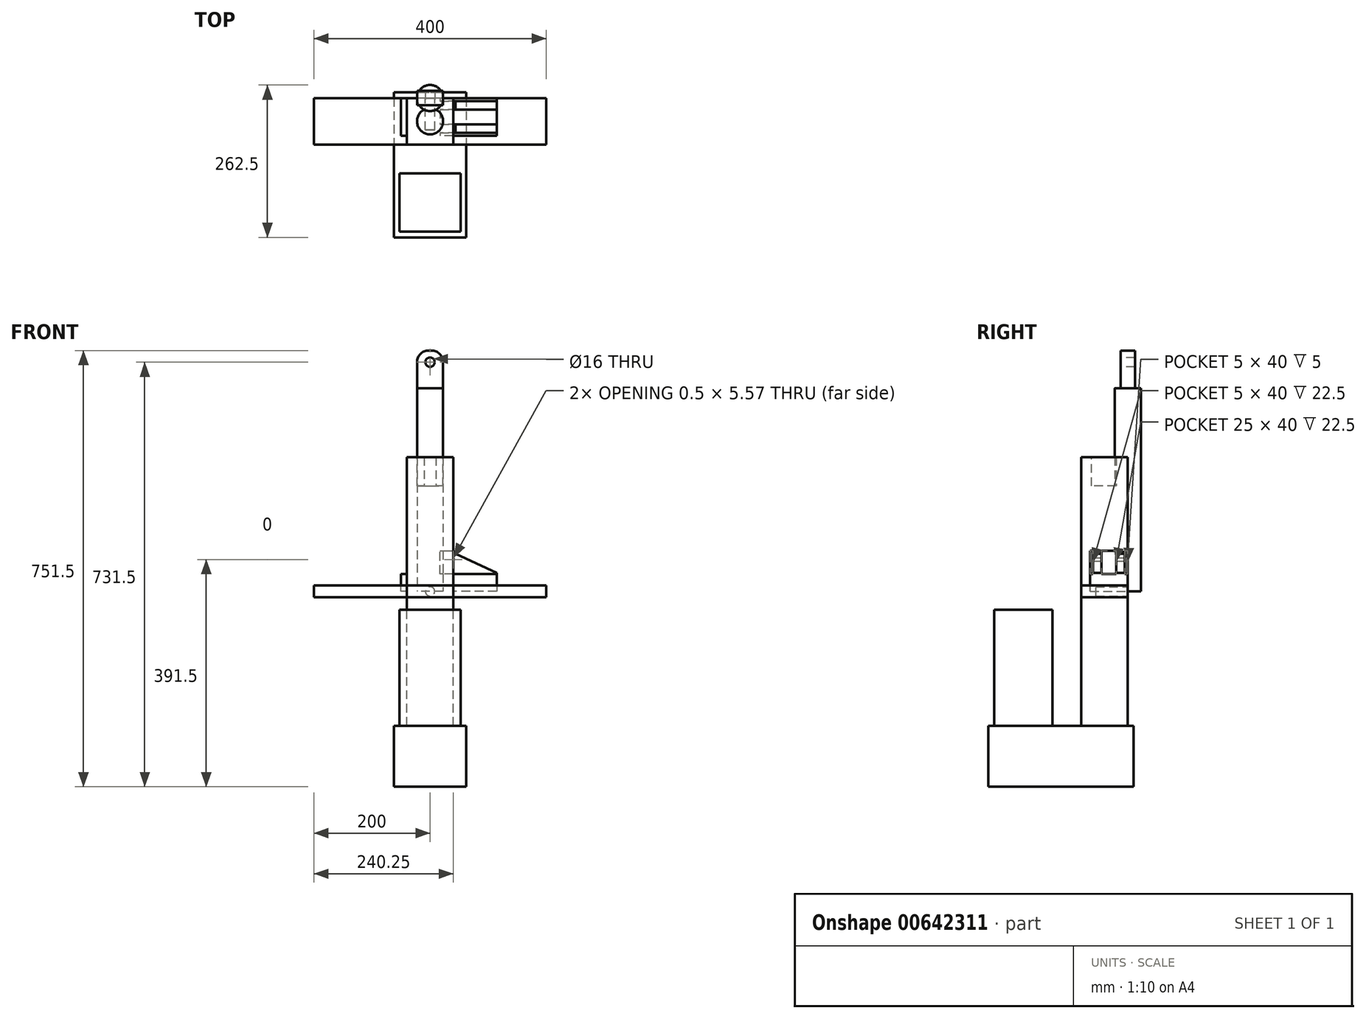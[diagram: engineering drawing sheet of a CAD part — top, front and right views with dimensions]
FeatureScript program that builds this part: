
annotation { "Feature Type Name" : "Feature", "Feature Type Description" : "" }
export const myFeature = defineFeature(function(context is Context, id is Id, definition is map)
    precondition{}
    {
        {
            var Q0;
            Q0=qCreatedBy(makeId("Front.planeOp"),FACE);
            var sketch = newSketch(context, id + "F0", { "sketchPlane" : qUnion([Q0])});
            skLineSegment(sketch, "E0.bottom", {"start": v(40, -231.5) * mm, "end": v(-40, -231.5) * mm});
            skLineSegment(sketch, "E0.top", {"start": v(40, 231.5) * mm, "end": v(-40, 231.5) * mm});
            skLineSegment(sketch, "E0.left", {"start": v(40, -231.5) * mm, "end": v(40, 231.5) * mm});
            skLineSegment(sketch, "E0.right", {"start": v(-40, -231.5) * mm, "end": v(-40, 231.5) * mm});
            skPoint(sketch, "E0.middle", {"position": v(0, 0) * mm});
            skSolve(sketch);
        }
        {
            var Q0;
            Q0=makeQuery(id+"F0.imprint","IMPRINT",FACE,{"disambiguationData":[TD([[makeQuery(id+"F0.imprint","IMPRINT",EDGE,{"derivedFrom":sQuery(id+"F0.wireOp",EDGE,"E0.bottom")}),-1.0]])]});
            extrude(context, id + "F1", {"entities" : qUnion([Q0]), "depth" : 80 * mm, "offsetDistance" : 25 * mm});
        }
        {
            var Q0;
            Q0=makeQuery(id+"F1.opExtrude","SWEPT_FACE",FACE,{"disambiguationData":[OSD([sQuery(id+"F0.wireOp",EDGE,"E0.bottom")])]});
            var sketch = newSketch(context, id + "F2", { "sketchPlane" : qUnion([Q0])});
            skLineSegment(sketch, "E1.bottom", {"start": v(-62.5, 0) * mm, "end": v(62.5, 0) * mm});
            skLineSegment(sketch, "E1.top", {"start": v(-62.5, 240) * mm, "end": v(62.5, 240) * mm});
            skLineSegment(sketch, "E1.left", {"start": v(-62.5, 0) * mm, "end": v(-62.5, 240) * mm});
            skLineSegment(sketch, "E1.right", {"start": v(62.5, 0) * mm, "end": v(62.5, 240) * mm});
            skLineSegment(sketch, "E2.top", {"start": v(-62.5, -10) * mm, "end": v(62.5, -10) * mm});
            skLineSegment(sketch, "E2.left", {"start": v(-62.5, 0) * mm, "end": v(-62.5, -10) * mm});
            skLineSegment(sketch, "E2.right", {"start": v(62.5, 0) * mm, "end": v(62.5, -10) * mm});
            skSolve(sketch);
        }
        {
            var Q0;
            Q0=makeQuery(id+"F2.imprint","IMPRINT",FACE,{"disambiguationData":[TD([[makeQuery(id+"F2.imprint","IMPRINT",EDGE,{"derivedFrom":sQuery(id+"F2.wireOp",EDGE,"E1.top")}),-1.0]])]});
            var Q1;
            {var subQ1=sQuery(id+"F0.wireOp",EDGE,"E0.bottom");Q1=makeQuery(id+"F2.imprint","IMPRINT",FACE,{"disambiguationData":[TD([[makeQuery(id+"F2.imprint","IMPRINT",EDGE,{"derivedFrom":makeQuery(id+"F1.opExtrude","CAP_EDGE",EDGE,{"disambiguationData":[OSD([subQ1])],"isStart":false})}),1.0]])]});}
            var Q2;
            Q2=makeQuery(id+"F2.imprint","IMPRINT",FACE,{"disambiguationData":[TD([[makeQuery(id+"F2.imprint","IMPRINT",EDGE,{"derivedFrom":sQuery(id+"F2.wireOp",EDGE,"E2.top")}),1.0]])]});
            extrude(context, id + "F3", {"entities" : qUnion([Q0, Q1, Q2]), "operationType" : NewBodyOperationType.ADD, "depth" : 105 * mm, "offsetDistance" : 25 * mm});
        }
        {
            var Q0;
            Q0=makeQuery(id+"F3.opExtrude","CAP_FACE",FACE,{"disambiguationData":[OSD([sQuery(id+"F2.wireOp",EDGE,"E1.top"),sQuery(id+"F2.wireOp",EDGE,"E1.left"),sQuery(id+"F2.wireOp",EDGE,"E1.right"),sQuery(id+"F2.wireOp",EDGE,"E2.top"),sQuery(id+"F2.wireOp",EDGE,"E2.left"),sQuery(id+"F2.wireOp",EDGE,"E2.right")])],"isStart":true});
            var sketch = newSketch(context, id + "F4", { "sketchPlane" : qUnion([Q0])});
            skLineSegment(sketch, "E3.bottom", {"start": v(-52.5, -130) * mm, "end": v(52.5, -130) * mm});
            skLineSegment(sketch, "E3.top", {"start": v(-52.5, -230) * mm, "end": v(52.5, -230) * mm});
            skLineSegment(sketch, "E3.left", {"start": v(-52.5, -130) * mm, "end": v(-52.5, -230) * mm});
            skLineSegment(sketch, "E3.right", {"start": v(52.5, -130) * mm, "end": v(52.5, -230) * mm});
            skSolve(sketch);
        }
        {
            var Q0;
            Q0=makeQuery(id+"F4.imprint","IMPRINT",FACE,{"disambiguationData":[TD([[makeQuery(id+"F4.imprint","IMPRINT",EDGE,{"derivedFrom":sQuery(id+"F4.wireOp",EDGE,"E3.bottom")}),-1.0]])]});
            extrude(context, id + "F5", {"entities" : qUnion([Q0]), "operationType" : NewBodyOperationType.ADD, "depth" : 200 * mm, "offsetDistance" : 25 * mm});
        }
        {
            var Q0;
            Q0=makeQuery(id+"F1.opExtrude","SWEPT_FACE",FACE,{"disambiguationData":[OSD([sQuery(id+"F0.wireOp",EDGE,"E0.top")])]});
            var sketch = newSketch(context, id + "F6", { "sketchPlane" : qUnion([Q0])});
            skCircle(sketch, "E4", {"center": v(0, -40) * mm, "radius": 22.5 * mm});
            skPoint(sketch, "E4.centerSnap0", {"position": v(40, -40) * mm});
            skSolve(sketch);
        }
        {
            var Q0;
            Q0=makeQuery(id+"F6.imprint","IMPRINT",FACE,{"disambiguationData":[TD([[makeQuery(id+"F6.imprint","IMPRINT",EDGE,{"derivedFrom":sQuery(id+"F6.wireOp",EDGE,"E4")}),1.0]])]});
            extrude(context, id + "F7", {"entities" : qUnion([Q0]), "operationType" : NewBodyOperationType.REMOVE, "oppositeDirection" : true, "depth" : 50 * mm, "offsetDistance" : 25 * mm});
        }
        {
            var Q0;
            Q0=qCreatedBy(makeId("Top.planeOp"),FACE);
            var sketch = newSketch(context, id + "F8", { "sketchPlane" : qUnion([Q0])});
            skCircle(sketch, "E5", {"center": v(0, 0) * mm, "radius": 22.5 * mm});
            skSolve(sketch);
        }
        {
            var Q0;
            Q0=makeQuery(id+"F8.imprint","IMPRINT",FACE,{"disambiguationData":[TD([[makeQuery(id+"F8.imprint","IMPRINT",EDGE,{"derivedFrom":sQuery(id+"F8.wireOp",EDGE,"E5")}),1.0]])]});
            extrude(context, id + "F9", {"entities" : qUnion([Q0]), "depth" : 350 * mm, "offsetDistance" : 25 * mm});
        }
        {
            var Q0;
            Q0=makeQuery(id+"F9.opExtrude","CAP_FACE",FACE,{"disambiguationData":[OSD([sQuery(id+"F8.wireOp",EDGE,"E5")])],"isStart":false});
            var sketch = newSketch(context, id + "F10", { "sketchPlane" : qUnion([Q0])});
            skLineSegment(sketch, "E6.bottom", {"start": v(22.5, -12.5) * mm, "end": v(-22.5, -12.5) * mm});
            skLineSegment(sketch, "E6.top", {"start": v(22.5, 12.5) * mm, "end": v(-22.5, 12.5) * mm});
            skLineSegment(sketch, "E6.left", {"start": v(22.5, -12.5) * mm, "end": v(22.5, 12.5) * mm});
            skLineSegment(sketch, "E6.right", {"start": v(-22.5, -12.5) * mm, "end": v(-22.5, 12.5) * mm});
            skPoint(sketch, "E6.middle", {"position": v(0, 0) * mm});
            skSolve(sketch);
        }
        {
            var Q0;
            {var subQ0=sQuery(id+"F10.wireOp",EDGE,"E6.bottom");var subQ1=makeQuery(id+"F9.opExtrude","CAP_EDGE",EDGE,{"disambiguationData":[OSD([sQuery(id+"F8.wireOp",EDGE,"E5")])],"isStart":false});var subQ4=makeQuery(id+"F10.imprint","INTERSECT",VERTEX,{"disambiguationData":[OD(0.0)],"derivedFrom":[subQ1,subQ0]});Q0=makeQuery(id+"F10.imprint","IMPRINT",FACE,{"disambiguationData":[TD([[makeQuery(id+"F10.imprint","IMPRINT",EDGE,{"disambiguationData":[TD([[subQ4,-1.0]])],"derivedFrom":subQ0}),-1.0]])]});}
            var Q1;
            {var subQ0=sQuery(id+"F10.wireOp",EDGE,"E6.right");var subQ1=sQuery(id+"F10.wireOp",EDGE,"E6.top");var subQ2=makeQuery(id+"F10.imprint","INTERSECT",VERTEX,{"derivedFrom":[subQ1,subQ0]});Q1=makeQuery(id+"F10.imprint","IMPRINT",FACE,{"disambiguationData":[TD([[makeQuery(id+"F10.imprint","IMPRINT",EDGE,{"disambiguationData":[TD([[subQ2,1.0]])],"derivedFrom":subQ1}),1.0]])]});}
            var Q2;
            {var subQ0=sQuery(id+"F10.wireOp",EDGE,"E6.right");var subQ1=sQuery(id+"F10.wireOp",EDGE,"E6.bottom");var subQ2=makeQuery(id+"F10.imprint","INTERSECT",VERTEX,{"derivedFrom":[subQ1,subQ0]});Q2=makeQuery(id+"F10.imprint","IMPRINT",FACE,{"disambiguationData":[TD([[makeQuery(id+"F10.imprint","IMPRINT",EDGE,{"disambiguationData":[TD([[subQ2,1.0]])],"derivedFrom":subQ1}),-1.0]])]});}
            var Q3;
            {var subQ0=sQuery(id+"F10.wireOp",EDGE,"E6.left");var subQ1=sQuery(id+"F10.wireOp",EDGE,"E6.bottom");var subQ2=makeQuery(id+"F10.imprint","INTERSECT",VERTEX,{"derivedFrom":[subQ1,subQ0]});Q3=makeQuery(id+"F10.imprint","IMPRINT",FACE,{"disambiguationData":[TD([[makeQuery(id+"F10.imprint","IMPRINT",EDGE,{"disambiguationData":[TD([[subQ2,-1.0]])],"derivedFrom":subQ1}),-1.0]])]});}
            var Q4;
            {var subQ0=sQuery(id+"F10.wireOp",EDGE,"E6.left");var subQ1=sQuery(id+"F10.wireOp",EDGE,"E6.top");var subQ2=makeQuery(id+"F10.imprint","INTERSECT",VERTEX,{"derivedFrom":[subQ1,subQ0]});Q4=makeQuery(id+"F10.imprint","IMPRINT",FACE,{"disambiguationData":[TD([[makeQuery(id+"F10.imprint","IMPRINT",EDGE,{"disambiguationData":[TD([[subQ2,-1.0]])],"derivedFrom":subQ1}),1.0]])]});}
            extrude(context, id + "F11", {"entities" : qUnion([Q0, Q1, Q2, Q3, Q4]), "operationType" : NewBodyOperationType.ADD, "depth" : 65 * mm, "offsetDistance" : 25 * mm});
        }
        {
            var Q0;
            Q0=makeQuery(id+"F11.opExtrude","SWEPT_FACE",FACE,{"disambiguationData":[OSD([sQuery(id+"F10.wireOp",EDGE,"E6.bottom")])]});
            var sketch = newSketch(context, id + "F12", { "sketchPlane" : qUnion([Q0])});
            skCircle(sketch, "E7", {"center": v(0, 395) * mm, "radius": 8 * mm});
            skPoint(sketch, "E7.centerSnap0", {"position": v(0, 415) * mm});
            skSolve(sketch);
        }
        {
            var Q0;
            Q0=makeQuery(id+"F12.imprint","IMPRINT",FACE,{"disambiguationData":[TD([[makeQuery(id+"F12.imprint","IMPRINT",EDGE,{"derivedFrom":sQuery(id+"F12.wireOp",EDGE,"E7")}),1.0]])]});
            extrude(context, id + "F13", {"entities" : qUnion([Q0]), "operationType" : NewBodyOperationType.REMOVE, "endBound" : BoundingType.THROUGH_ALL, "oppositeDirection" : true, "depth" : 25 * mm, "offsetDistance" : 25 * mm});
        }
        {
            var Q0;
            Q0=makeQuery(id+"F11.opExtrude","CAP_EDGE",EDGE,{"disambiguationData":[OSD([sQuery(id+"F10.wireOp",EDGE,"E6.right")])],"isStart":false});
            var Q1;
            Q1=makeQuery(id+"F11.opExtrude","CAP_EDGE",EDGE,{"disambiguationData":[OSD([sQuery(id+"F10.wireOp",EDGE,"E6.left")])],"isStart":false});
            fillet(context, id + "F14", {"entities" : qUnion([Q0, Q1]), "radius" : 20 * mm, "tangentPropagation" : true, "allowEdgeOverflow" : false});
        }
        {
            var Q0;
            Q0=qCreatedBy(makeId("Front.planeOp"),FACE);
            var sketch = newSketch(context, id + "F15", { "sketchPlane" : qUnion([Q0])});
            skLineSegment(sketch, "E8", {"start": v(0, 0) * mm, "end": v(0, 30) * mm});
            skLineSegment(sketch, "E9", {"start": v(0, 30) * mm, "end": v(17.5, 30) * mm});
            skLineSegment(sketch, "E10", {"start": v(17.5, 30) * mm, "end": v(17.5, 70) * mm});
            skLineSegment(sketch, "E11", {"start": v(17.5, 70) * mm, "end": v(47.5, 70) * mm});
            skLineSegment(sketch, "E12", {"start": v(47.5, 70) * mm, "end": v(47.5, 30) * mm});
            skLineSegment(sketch, "E13", {"start": v(47.5, 30) * mm, "end": v(65, 30) * mm});
            skLineSegment(sketch, "E14", {"start": v(65, 30) * mm, "end": v(65, 0) * mm});
            skLineSegment(sketch, "E15", {"start": v(65, 0) * mm, "end": v(0, 0) * mm});
            skPoint(sketch, "E16", {"position": v(32.5, 70) * mm});
            skCircle(sketch, "E17", {"center": v(32.5, 55) * mm, "radius": 8 * mm});
            skSolve(sketch);
        }
        {
            var Q0;
            Q0=makeQuery(id+"F15.imprint","IMPRINT",FACE,{"disambiguationData":[TD([[makeQuery(id+"F15.imprint","IMPRINT",EDGE,{"derivedFrom":sQuery(id+"F15.wireOp",EDGE,"E8")}),-1.0]])]});
            extrude(context, id + "F16", {"entities" : qUnion([Q0]), "depth" : 65 * mm, "offsetDistance" : 25 * mm});
        }
        {
            var Q0;
            Q0=makeQuery(id+"F16.opExtrude","SWEPT_FACE",FACE,{"disambiguationData":[OSD([sQuery(id+"F15.wireOp",EDGE,"E11")])]});
            var sketch = newSketch(context, id + "F17", { "sketchPlane" : qUnion([Q0])});
            skLineSegment(sketch, "E18.bottom", {"start": v(17.5, -5) * mm, "end": v(47.5, -5) * mm});
            skLineSegment(sketch, "E18.top", {"start": v(17.5, -20) * mm, "end": v(47.5, -20) * mm});
            skLineSegment(sketch, "E18.left", {"start": v(17.5, -5) * mm, "end": v(17.5, -20) * mm});
            skLineSegment(sketch, "E18.right", {"start": v(47.5, -5) * mm, "end": v(47.5, -20) * mm});
            skLineSegment(sketch, "E19.bottom", {"start": v(17.5, -45) * mm, "end": v(47.5, -45) * mm});
            skLineSegment(sketch, "E19.top", {"start": v(17.5, -60) * mm, "end": v(47.5, -60) * mm});
            skLineSegment(sketch, "E19.left", {"start": v(17.5, -45) * mm, "end": v(17.5, -60) * mm});
            skLineSegment(sketch, "E19.right", {"start": v(47.5, -45) * mm, "end": v(47.5, -60) * mm});
            skSolve(sketch);
        }
        {
            var Q0;
            {var subQ0=sQuery(id+"F17.wireOp",EDGE,"E18.bottom");Q0=makeQuery(id+"F17.imprint","IMPRINT",FACE,{"disambiguationData":[TD([[makeQuery(id+"F17.imprint","IMPRINT",EDGE,{"derivedFrom":subQ0}),1.0]])]});}
            var Q1;
            {var subQ0=sQuery(id+"F17.wireOp",EDGE,"E18.top");Q1=makeQuery(id+"F17.imprint","IMPRINT",FACE,{"disambiguationData":[TD([[makeQuery(id+"F17.imprint","IMPRINT",EDGE,{"derivedFrom":subQ0}),-1.0]])]});}
            var Q2;
            {var subQ0=sQuery(id+"F17.wireOp",EDGE,"E19.top");Q2=makeQuery(id+"F17.imprint","IMPRINT",FACE,{"disambiguationData":[TD([[makeQuery(id+"F17.imprint","IMPRINT",EDGE,{"derivedFrom":subQ0}),-1.0]])]});}
            var Q3;
            Q3=makeQuery(id+"F16.opExtrude","SWEPT_FACE",FACE,{"disambiguationData":[OSD([sQuery(id+"F15.wireOp",EDGE,"E9")])]});
            extrude(context, id + "F18", {"entities" : qUnion([Q0, Q1, Q2]), "operationType" : NewBodyOperationType.REMOVE, "endBound" : BoundingType.UP_TO_SURFACE, "oppositeDirection" : true, "depth" : 25 * mm, "endBoundEntityFace" : qUnion([Q3]), "offsetDistance" : 25 * mm});
        }
        {
            var Q0;
            {var subQ0=sQuery(id+"F15.wireOp",EDGE,"E10");var subQ1=sQuery(id+"F15.wireOp",EDGE,"E11");Q0=makeQuery(id+"F18.boolean.opBoolean","SPLIT",EDGE,{"disambiguationData":[TD([makeQuery(id+"F18.opExtrude","SWEPT_FACE",FACE,{"disambiguationData":[OSD([sQuery(id+"F17.wireOp",EDGE,"E18.bottom")])]})])],"derivedFrom":makeQuery(id+"F16.opExtrude","SWEPT_EDGE",EDGE,{"disambiguationData":[OSD([subQ0,subQ1])]})});}
            var Q1;
            {var subQ0=sQuery(id+"F15.wireOp",EDGE,"E10");var subQ1=sQuery(id+"F15.wireOp",EDGE,"E11");Q1=makeQuery(id+"F18.boolean.opBoolean","SPLIT",EDGE,{"disambiguationData":[TD([makeQuery(id+"F18.opExtrude","SWEPT_FACE",FACE,{"disambiguationData":[OSD([sQuery(id+"F17.wireOp",EDGE,"E19.bottom")])]})])],"derivedFrom":makeQuery(id+"F16.opExtrude","SWEPT_EDGE",EDGE,{"disambiguationData":[OSD([subQ0,subQ1])]})});}
            var Q2;
            {var subQ0=sQuery(id+"F15.wireOp",EDGE,"E11");var subQ1=sQuery(id+"F15.wireOp",EDGE,"E12");Q2=makeQuery(id+"F18.boolean.opBoolean","SPLIT",EDGE,{"disambiguationData":[TD([makeQuery(id+"F18.opExtrude","SWEPT_FACE",FACE,{"disambiguationData":[OSD([sQuery(id+"F17.wireOp",EDGE,"E19.bottom")])]})])],"derivedFrom":makeQuery(id+"F16.opExtrude","SWEPT_EDGE",EDGE,{"disambiguationData":[OSD([subQ0,subQ1])]})});}
            var Q3;
            {var subQ0=sQuery(id+"F15.wireOp",EDGE,"E11");var subQ1=sQuery(id+"F15.wireOp",EDGE,"E12");Q3=makeQuery(id+"F18.boolean.opBoolean","SPLIT",EDGE,{"disambiguationData":[TD([makeQuery(id+"F18.opExtrude","SWEPT_FACE",FACE,{"disambiguationData":[OSD([sQuery(id+"F17.wireOp",EDGE,"E18.bottom")])]})])],"derivedFrom":makeQuery(id+"F16.opExtrude","SWEPT_EDGE",EDGE,{"disambiguationData":[OSD([subQ0,subQ1])]})});}
            fillet(context, id + "F19", {"entities" : qUnion([Q0, Q1, Q2, Q3]), "radius" : 15 * mm, "tangentPropagation" : true, "allowEdgeOverflow" : false});
        }
        {
            var Q0;
            Q0=makeQuery(id+"F16.opExtrude","SWEPT_FACE",FACE,{"disambiguationData":[OSD([sQuery(id+"F15.wireOp",EDGE,"E14")])]});
            extrude(context, id + "F20", {"entities" : qUnion([Q0]), "operationType" : NewBodyOperationType.ADD, "depth" : 50 * mm, "offsetDistance" : 25 * mm});
        }
        {
            var Q0;
            Q0=makeQuery(id+"F16.opExtrude","SWEPT_FACE",FACE,{"disambiguationData":[OSD([sQuery(id+"F15.wireOp",EDGE,"E8")])]});
            extrude(context, id + "F21", {"entities" : qUnion([Q0]), "operationType" : NewBodyOperationType.ADD, "depth" : 50 * mm, "offsetDistance" : 25 * mm});
        }
        {
            var Q0;
            Q0=qCreatedBy(makeId("Front.planeOp"),FACE);
            var sketch = newSketch(context, id + "F22", { "sketchPlane" : qUnion([Q0])});
            skCircle(sketch, "E20", {"center": v(0, 0) * mm, "radius": 8 * mm});
            skSolve(sketch);
        }
        {
            var Q0;
            Q0=makeQuery(id+"F22.imprint","IMPRINT",FACE,{"disambiguationData":[TD([[makeQuery(id+"F22.imprint","IMPRINT",EDGE,{"derivedFrom":sQuery(id+"F22.wireOp",EDGE,"E20")}),1.0]])]});
            extrude(context, id + "F23", {"entities" : qUnion([Q0]), "depth" : 55 * mm, "offsetDistance" : 25 * mm});
        }
        {
            var Q0;
            {var subQ1=sQuery(id+"F15.wireOp",EDGE,"E13");var subQ2=sQuery(id+"F15.wireOp",EDGE,"E12");Q0=makeQuery(id+"F18.boolean.opBoolean","SPLIT",EDGE,{"disambiguationData":[TD([makeQuery(id+"F18.opExtrude","SWEPT_FACE",FACE,{"disambiguationData":[OSD([sQuery(id+"F17.wireOp",EDGE,"E19.bottom")])]})])],"derivedFrom":makeQuery(id+"F16.opExtrude","SWEPT_EDGE",EDGE,{"disambiguationData":[OSD([subQ2,subQ1])]})});}
            var Q1;
            {var subQ0=sQuery(id+"F15.wireOp",EDGE,"E13");var subQ2=sQuery(id+"F15.wireOp",EDGE,"E12");Q1=makeQuery(id+"F18.boolean.opBoolean","SPLIT",EDGE,{"disambiguationData":[TD([makeQuery(id+"F18.opExtrude","SWEPT_FACE",FACE,{"disambiguationData":[OSD([sQuery(id+"F17.wireOp",EDGE,"E18.bottom")])]})])],"derivedFrom":makeQuery(id+"F16.opExtrude","SWEPT_EDGE",EDGE,{"disambiguationData":[OSD([subQ2,subQ0])]})});}
            var Q2;
            {var subQ0=sQuery(id+"F15.wireOp",EDGE,"E9");var subQ1=sQuery(id+"F15.wireOp",EDGE,"E10");Q2=makeQuery(id+"F18.boolean.opBoolean","SPLIT",EDGE,{"disambiguationData":[TD([makeQuery(id+"F18.opExtrude","SWEPT_FACE",FACE,{"disambiguationData":[OSD([sQuery(id+"F17.wireOp",EDGE,"E19.bottom")])]})])],"derivedFrom":makeQuery(id+"F16.opExtrude","SWEPT_EDGE",EDGE,{"disambiguationData":[OSD([subQ0,subQ1])]})});}
            var Q3;
            {var subQ0=sQuery(id+"F15.wireOp",EDGE,"E9");var subQ1=sQuery(id+"F15.wireOp",EDGE,"E10");Q3=makeQuery(id+"F18.boolean.opBoolean","SPLIT",EDGE,{"disambiguationData":[TD([makeQuery(id+"F18.opExtrude","SWEPT_FACE",FACE,{"disambiguationData":[OSD([sQuery(id+"F17.wireOp",EDGE,"E18.bottom")])]})])],"derivedFrom":makeQuery(id+"F16.opExtrude","SWEPT_EDGE",EDGE,{"disambiguationData":[OSD([subQ0,subQ1])]})});}
            chamfer(context, id + "F24", {"entities" : qUnion([Q0, Q1, Q2, Q3]), "width" : 100 * mm, "tangentPropagation" : true});
        }
        {
            var Q0;
            Q0=qCreatedBy(makeId("Front.planeOp"),FACE);
            var sketch = newSketch(context, id + "F25", { "sketchPlane" : qUnion([Q0])});
            skLineSegment(sketch, "E21.bottom", {"start": v(200, -10) * mm, "end": v(-200, -10) * mm});
            skLineSegment(sketch, "E21.top", {"start": v(200, 10) * mm, "end": v(-200, 10) * mm});
            skLineSegment(sketch, "E21.left", {"start": v(200, -10) * mm, "end": v(200, 10) * mm});
            skLineSegment(sketch, "E21.right", {"start": v(-200, -10) * mm, "end": v(-200, 10) * mm});
            skPoint(sketch, "E21.middle", {"position": v(0, 0) * mm});
            skSolve(sketch);
        }
        {
            var Q0;
            Q0=makeQuery(id+"F25.imprint","IMPRINT",FACE,{"disambiguationData":[TD([[makeQuery(id+"F25.imprint","IMPRINT",EDGE,{"derivedFrom":sQuery(id+"F25.wireOp",EDGE,"E21.bottom")}),-1.0]])]});
            extrude(context, id + "F26", {"entities" : qUnion([Q0]), "depth" : 80 * mm, "offsetDistance" : 25 * mm});
        }
    });
